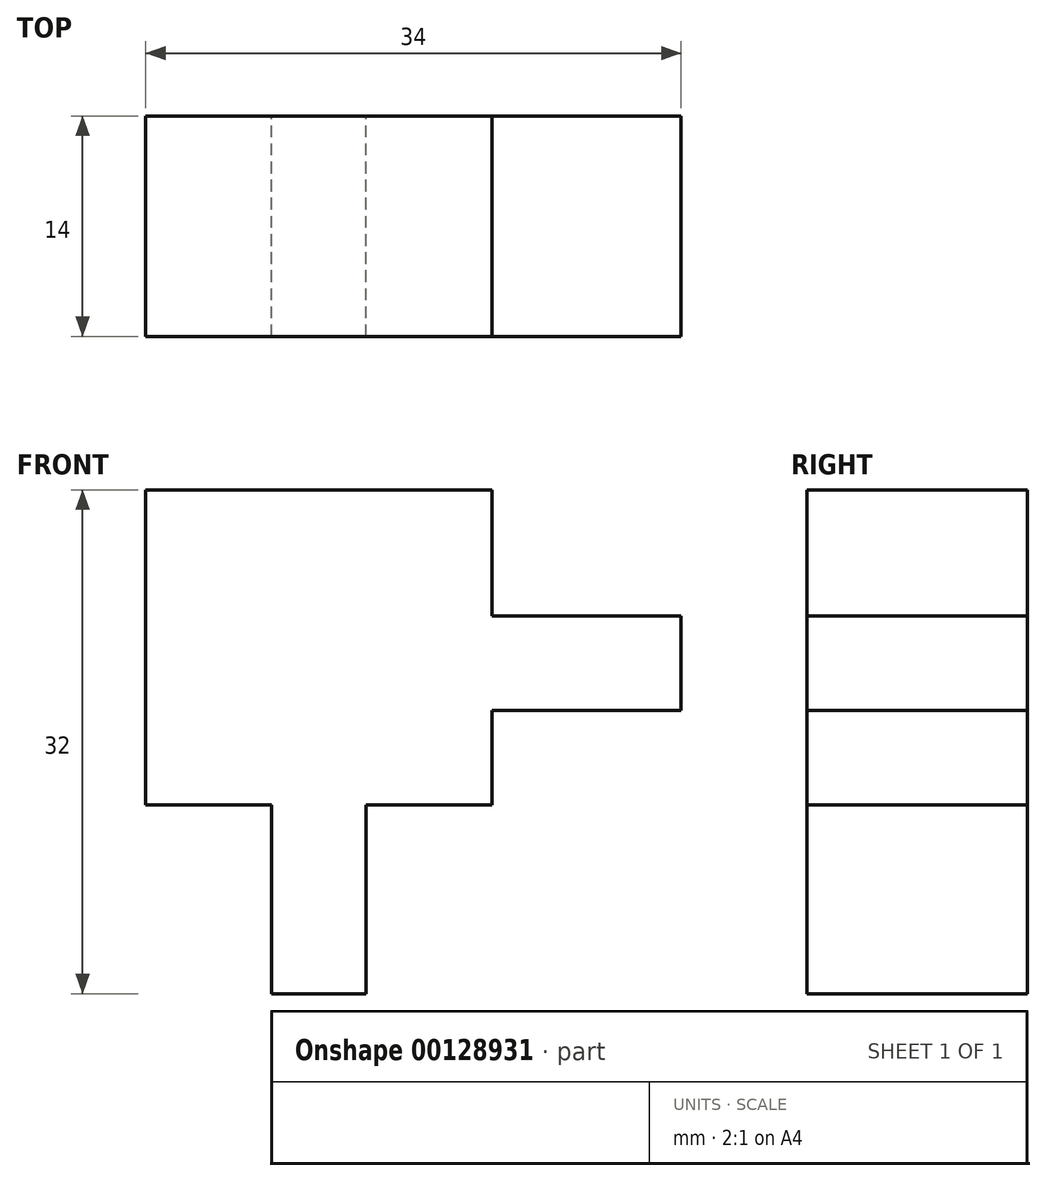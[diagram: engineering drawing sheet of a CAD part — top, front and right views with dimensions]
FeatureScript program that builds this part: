
annotation { "Feature Type Name" : "Feature", "Feature Type Description" : "" }
export const myFeature = defineFeature(function(context is Context, id is Id, definition is map)
    precondition{}
    {
        {
            var Q0;
            Q0=qCreatedBy(makeId("Front.planeOp"),FACE);
            var sketch = newSketch(context, id + "F0", { "sketchPlane" : qUnion([Q0])});
            skLineSegment(sketch, "E0", {"start": v(-8, 4.16) * mm, "end": v(0, 4.16) * mm});
            skLineSegment(sketch, "E1", {"start": v(0, 4.16) * mm, "end": v(0, -7.84) * mm});
            skLineSegment(sketch, "E2", {"start": v(0, -7.84) * mm, "end": v(6, -7.84) * mm});
            skLineSegment(sketch, "E3", {"start": v(6, -7.84) * mm, "end": v(6, 4.16) * mm});
            skLineSegment(sketch, "E4", {"start": v(6, 4.16) * mm, "end": v(14, 4.16) * mm});
            skLineSegment(sketch, "E5", {"start": v(-8, 24.16) * mm, "end": v(14, 24.16) * mm});
            skLineSegment(sketch, "E6", {"start": v(-8, 24.16) * mm, "end": v(-8, 4.16) * mm});
            skLineSegment(sketch, "E7", {"start": v(14, 24.16) * mm, "end": v(14, 16.16) * mm});
            skLineSegment(sketch, "E8", {"start": v(14, 16.16) * mm, "end": v(26, 16.16) * mm});
            skLineSegment(sketch, "E9", {"start": v(26, 16.16) * mm, "end": v(26, 10.16) * mm});
            skLineSegment(sketch, "E10", {"start": v(26, 10.16) * mm, "end": v(14, 10.16) * mm});
            skLineSegment(sketch, "E11", {"start": v(14, 10.16) * mm, "end": v(14, 4.16) * mm});
            skSolve(sketch);
        }
        {
            var Q0;
            Q0=makeQuery(id+"F0.imprint","IMPRINT",FACE,{"disambiguationData":[TD([[makeQuery(id+"F0.imprint","IMPRINT",EDGE,{"derivedFrom":sQuery(id+"F0.wireOp",EDGE,"E0")}),1.0]])]});
            extrude(context, id + "F1", {"entities" : qUnion([Q0]), "depth" : 14 * mm});
        }
    });
